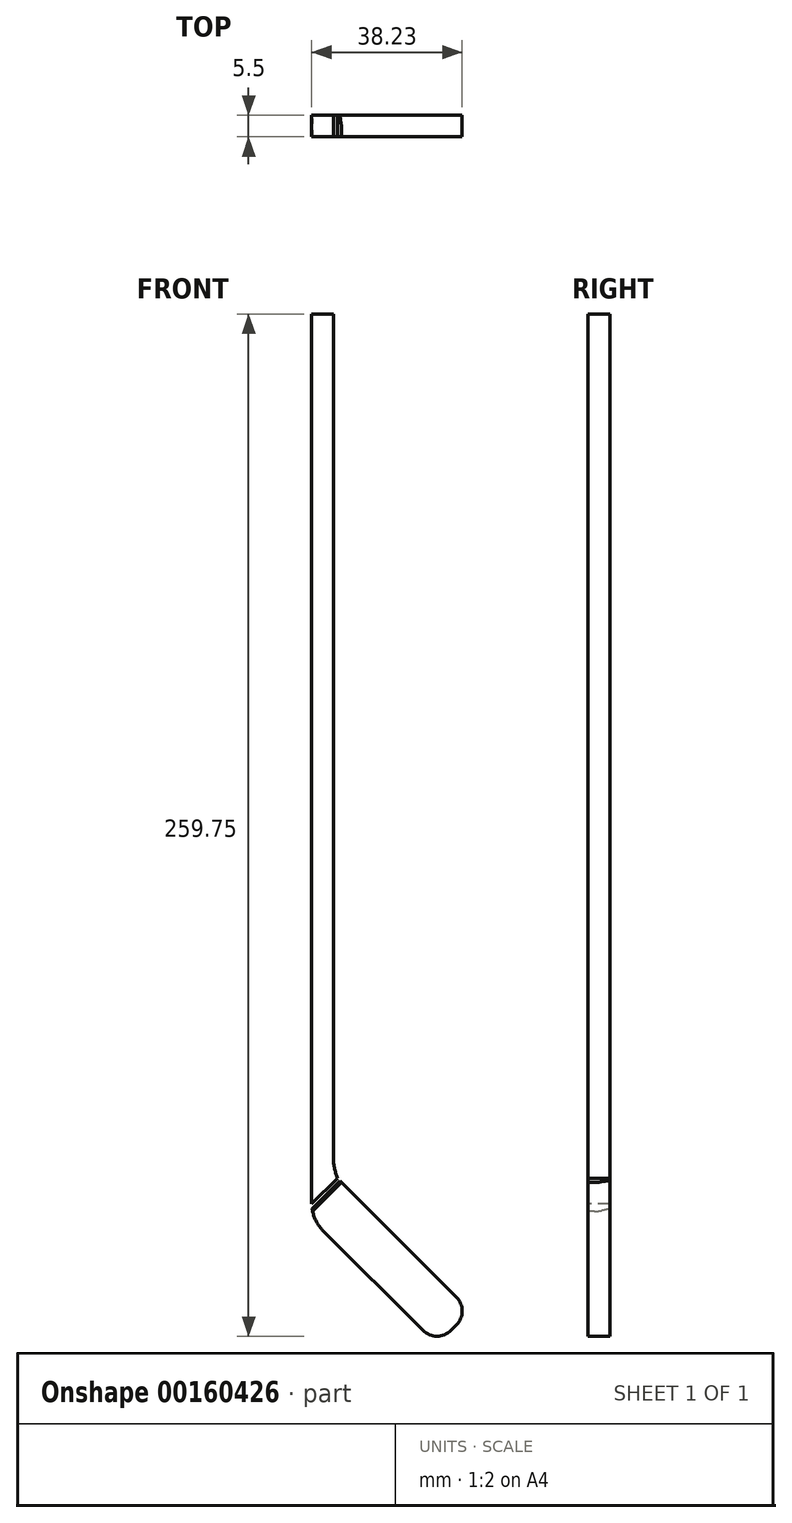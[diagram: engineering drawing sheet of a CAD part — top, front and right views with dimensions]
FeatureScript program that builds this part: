
annotation { "Feature Type Name" : "Feature", "Feature Type Description" : "" }
export const myFeature = defineFeature(function(context is Context, id is Id, definition is map)
    precondition{}
    {
        {
            var Q0;
            Q0=qCreatedBy(makeId("Front.planeOp"),FACE);
            var sketch = newSketch(context, id + "F0", { "sketchPlane" : qUnion([Q0])});
            skLineSegment(sketch, "E0", {"start": v(0, 0) * mm, "end": v(0, 230) * mm});
            skLineSegment(sketch, "E1", {"start": v(0, 230) * mm, "end": v(5.5, 230) * mm});
            skLineSegment(sketch, "E2", {"start": v(0, 0) * mm, "end": v(31.82, -31.82) * mm});
            skLineSegment(sketch, "E3", {"start": v(31.82, -31.82) * mm, "end": v(40.3, -23.33) * mm});
            skLineSegment(sketch, "E4", {"start": v(5.5, 11.47) * mm, "end": v(5.5, 230) * mm});
            skLineSegment(sketch, "E5", {"start": v(5.5, 11.47) * mm, "end": v(40.3, -23.33) * mm});
            skSolve(sketch);
        }
        {
            var Q0;
            Q0=makeQuery(id+"F0.imprint","IMPRINT",FACE,{"disambiguationData":[TD([[makeQuery(id+"F0.imprint","IMPRINT",EDGE,{"derivedFrom":sQuery(id+"F0.wireOp",EDGE,"E0")}),-1.0]])]});
            extrude(context, id + "F1", {"entities" : qUnion([Q0]), "endBound" : BoundingType.SYMMETRIC, "depth" : 5.5 * mm});
        }
        {
            var Q0;
            Q0=makeQuery(id+"F1.opExtrude","SWEPT_EDGE",EDGE,{"disambiguationData":[OSD([sQuery(id+"F0.wireOp",EDGE,"E2"),sQuery(id+"F0.wireOp",EDGE,"E3")])]});
            var Q1;
            Q1=makeQuery(id+"F1.opExtrude","SWEPT_EDGE",EDGE,{"disambiguationData":[OSD([sQuery(id+"F0.wireOp",EDGE,"E3"),sQuery(id+"F0.wireOp",EDGE,"fwePRi2J-oRte-dWRm-7DaZ-aHYD94WTmia1")])]});
            fillet(context, id + "F2", {"entities" : qUnion([Q0, Q1]), "radius" : 5 * mm, "tangentPropagation" : true, "allowEdgeOverflow" : false});
        }
        {
            var Q0;
            Q0=makeQuery(id+"F1.opExtrude","SWEPT_EDGE",EDGE,{"disambiguationData":[OSD([sQuery(id+"F0.wireOp",EDGE,"E0"),sQuery(id+"F0.wireOp",EDGE,"E2")])]});
            fillet(context, id + "F3", {"entities" : qUnion([Q0]), "radius" : 10 * mm, "tangentPropagation" : true, "allowEdgeOverflow" : false});
        }
        {
            var Q0;
            Q0=makeQuery(id+"F1.opExtrude","SWEPT_FACE",FACE,{"disambiguationData":[OSD([sQuery(id+"F0.wireOp",EDGE,"E2")])]});
            cPlane(context, id + "F4", {"entities" : qUnion([Q0]), "cplaneType" : CPlaneType.OFFSET, "offset" : 0 * mm, "width" : 150 * mm, "height" : 150 * mm});
        }
        {
            var Q0;
            Q0=qCreatedBy(id+"F4.planeOp",FACE);
            var sketch = newSketch(context, id + "F5", { "sketchPlane" : qUnion([Q0])});
            skPoint(sketch, "E6.0.3.end.orphan", {"position": v(45, 2.75) * mm});
            skPoint(sketch, "E6.0.3.start.orphan", {"position": v(45, -2.75) * mm});
            skPoint(sketch, "E6.0.1.start.orphan", {"position": v(45, 2.75) * mm});
            skLineSegment(sketch, "E7.0", {"start": v(-8.27, 2.75) * mm, "end": v(40, 2.75) * mm});
            skLineSegment(sketch, "E8.0", {"start": v(40, 2.75) * mm, "end": v(45, 2.75) * mm});
            skPoint(sketch, "E9.orphan", {"position": v(45, 4.91) * mm});
            skPoint(sketch, "E10.end.orphan", {"position": v(45, 0) * mm});
            skPoint(sketch, "E11.orphan", {"position": v(45, -16.43) * mm});
            skLineSegment(sketch, "E12", {"start": v(45, 1.25) * mm, "end": v(0.23, 1.25) * mm});
            skPoint(sketch, "E13.end.orphan", {"position": v(5, 0) * mm});
            skPoint(sketch, "E14.orphan", {"position": v(-162.63, 2.75) * mm});
            skLineSegment(sketch, "E15", {"start": v(45, 2.75) * mm, "end": v(45, 1.25) * mm});
            skPoint(sketch, "E16.orphan", {"position": v(45.8, 1.25) * mm});
            skLineSegment(sketch, "E17", {"start": v(0.23, 1.25) * mm, "end": v(-8.27, 2.75) * mm});
            skPoint(sketch, "E18.0.start.orphan", {"position": v(-2.93, 2.75) * mm});
            skPoint(sketch, "E19.orphan", {"position": v(4.14, 2.75) * mm});
            skSolve(sketch);
        }
        {
            var Q0;
            Q0 = qSketchRegion(id + "F5", true);
            extrude(context, id + "F6", {"entities" : qUnion([Q0]), "operationType" : NewBodyOperationType.REMOVE, "oppositeDirection" : true, "depth" : 31.75 * mm});
        }
        {
            var Q0;
            Q0=makeQuery(id+"F1.opExtrude","SWEPT_EDGE",EDGE,{"disambiguationData":[OSD([sQuery(id+"F0.wireOp",EDGE,"E4"),sQuery(id+"F0.wireOp",EDGE,"E5")])]});
            fillet(context, id + "F7", {"entities" : qUnion([Q0]), "radius" : 15 * mm, "tangentPropagation" : true, "allowEdgeOverflow" : false});
        }
        {
            var Q0;
            Q0=makeQuery(id+"F6.boolean.opBoolean","COPY",EDGE,{"derivedFrom":makeQuery(id+"F6.opExtrude","SWEPT_EDGE",EDGE,{"disambiguationData":[OSD([sQuery(id+"F5.wireOp",EDGE,"E7.0"),sQuery(id+"F5.wireOp",EDGE,"E17")])]})});
            var Q1;
            Q1=makeQuery(id+"F6.boolean.opBoolean","COPY",EDGE,{"derivedFrom":makeQuery(id+"F6.opExtrude","SWEPT_EDGE",EDGE,{"disambiguationData":[OSD([sQuery(id+"F5.wireOp",EDGE,"E12"),sQuery(id+"F5.wireOp",EDGE,"E17")])]})});
            fillet(context, id + "F8", {"entities" : qUnion([Q0, Q1]), "radius" : 10 * mm, "tangentPropagation" : true, "allowEdgeOverflow" : false});
        }
    });
